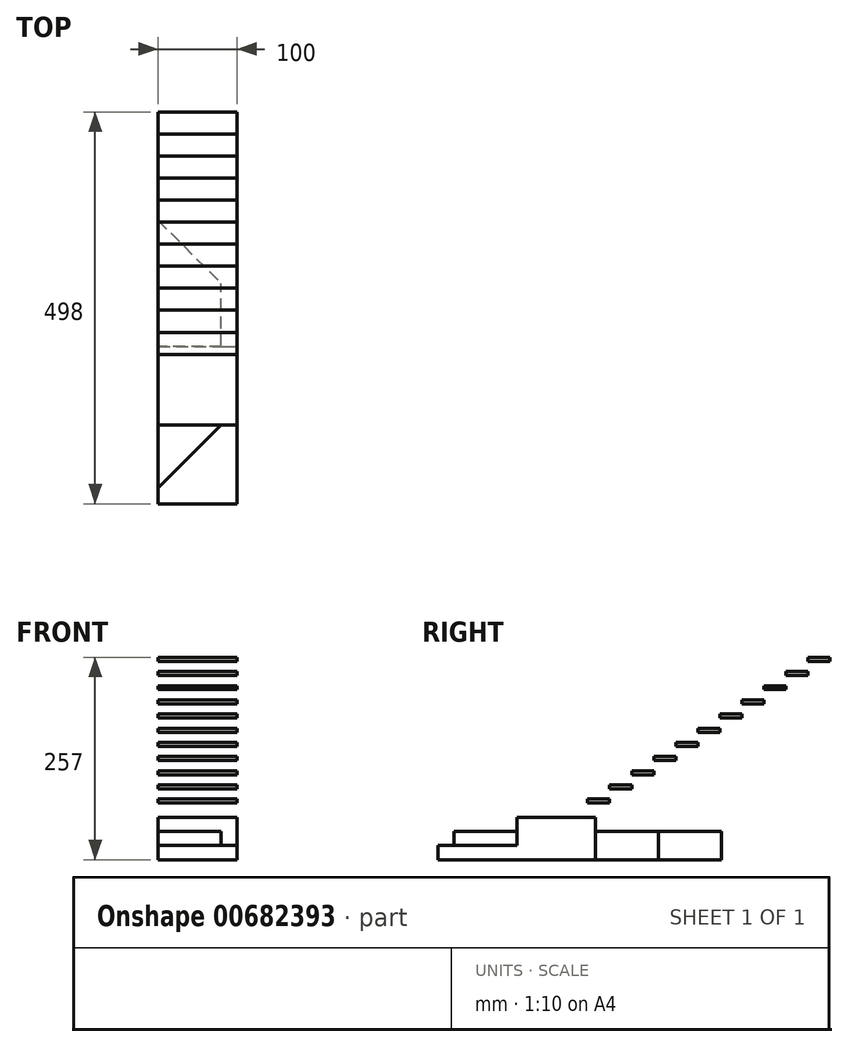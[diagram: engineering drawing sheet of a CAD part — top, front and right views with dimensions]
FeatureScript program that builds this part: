
annotation { "Feature Type Name" : "Feature", "Feature Type Description" : "" }
export const myFeature = defineFeature(function(context is Context, id is Id, definition is map)
    precondition{}
    {
        {
            var Q0;
            Q0=qCreatedBy(makeId("Right.planeOp"),FACE);
            var sketch = newSketch(context, id + "F0", { "sketchPlane" : qUnion([Q0])});
            skLineSegment(sketch, "E0.MirrorCS", {"start": v(-170, 0) * mm, "end": v(-170, 36) * mm});
            skLineSegment(sketch, "E1.MirrorCS", {"start": v(-170, 0) * mm, "end": v(0, 0) * mm});
            skLineSegment(sketch, "E2.MirrorCS", {"start": v(0, 36) * mm, "end": v(-170, 36) * mm});
            skPoint(sketch, "E3.bottom.end.orphan", {"position": v(133.33, 45) * mm});
            skPoint(sketch, "E4.left.start.orphan", {"position": v(133.33, 9) * mm});
            skPoint(sketch, "E5.right.start.orphan", {"position": v(122.85, 16.55) * mm});
            skPoint(sketch, "E5.top.end.orphan", {"position": v(122.85, 24.1) * mm});
            skPoint(sketch, "E6.right.start.orphan", {"position": v(112.37, 24.1) * mm});
            skPoint(sketch, "E6.top.end.orphan", {"position": v(112.37, 45) * mm});
            skPoint(sketch, "E7.MirrorCS.end.orphan", {"position": v(-112.37, 36) * mm});
            skPoint(sketch, "E7.MirrorCS.start.orphan", {"position": v(-112.37, 24.1) * mm});
            skPoint(sketch, "E8.MirrorCS.end.orphan", {"position": v(-122.85, 24.1) * mm});
            skPoint(sketch, "E9.MirrorCS.end.orphan", {"position": v(-122.85, 16.55) * mm});
            skPoint(sketch, "E10.MirrorCS.start.orphan", {"position": v(0, 24.1) * mm});
            skLineSegment(sketch, "E11.MirrorCS", {"start": v(0, 36) * mm, "end": v(170, 36) * mm});
            skLineSegment(sketch, "E12.MirrorCS", {"start": v(170, 0) * mm, "end": v(0, 0) * mm});
            skLineSegment(sketch, "E13.MirrorCS", {"start": v(170, 0) * mm, "end": v(170, 36) * mm});
            skSolve(sketch);
        }
        {
            var Q0;
            Q0=qSketchRegion(id+"F0",true);
            extrude(context, id + "F1", {"entities" : qUnion([Q0]), "oppositeDirection" : true, "depth" : 100 * mm, "offsetDistance" : 25 * mm, "hasSecondDirection" : true, "secondDirectionOppositeDirection" : true, "secondDirectionDepth" : 20 * mm});
        }
        {
            var Q0;
            Q0=qCreatedBy(makeId("Right.planeOp"),FACE);
            var sketch = newSketch(context, id + "F2", { "sketchPlane" : qUnion([Q0])});
            skLineSegment(sketch, "E14", {"start": v(0, 72) * mm, "end": v(28, 72) * mm});
            skLineSegment(sketch, "E15", {"start": v(28, 72) * mm, "end": v(28, 90) * mm, "construction": true});
            skLineSegment(sketch, "E16", {"start": v(28, 90) * mm, "end": v(56, 90) * mm});
            skLineSegment(sketch, "E17", {"start": v(56, 90) * mm, "end": v(56, 108) * mm, "construction": true});
            skLineSegment(sketch, "E18", {"start": v(56, 108) * mm, "end": v(84, 108) * mm});
            skLineSegment(sketch, "E19", {"start": v(84, 108) * mm, "end": v(84, 126) * mm, "construction": true});
            skLineSegment(sketch, "E20", {"start": v(84, 126) * mm, "end": v(112, 126) * mm});
            skLineSegment(sketch, "E21", {"start": v(112, 126) * mm, "end": v(112, 144) * mm, "construction": true});
            skLineSegment(sketch, "E22", {"start": v(112, 144) * mm, "end": v(140, 144) * mm});
            skLineSegment(sketch, "E23", {"start": v(140, 144) * mm, "end": v(140, 162) * mm, "construction": true});
            skLineSegment(sketch, "E24", {"start": v(140, 162) * mm, "end": v(168, 162) * mm});
            skLineSegment(sketch, "E25", {"start": v(168, 162) * mm, "end": v(168, 180) * mm, "construction": true});
            skLineSegment(sketch, "E26", {"start": v(168, 180) * mm, "end": v(196, 180) * mm});
            skLineSegment(sketch, "E27", {"start": v(196, 180) * mm, "end": v(196, 198) * mm, "construction": true});
            skLineSegment(sketch, "E28", {"start": v(196, 198) * mm, "end": v(224, 198) * mm});
            skLineSegment(sketch, "E29", {"start": v(224, 198) * mm, "end": v(224, 216) * mm, "construction": true});
            skLineSegment(sketch, "E30", {"start": v(224, 216) * mm, "end": v(252, 216) * mm});
            skLineSegment(sketch, "E31", {"start": v(252, 216) * mm, "end": v(252, 234) * mm, "construction": true});
            skLineSegment(sketch, "E32", {"start": v(252, 234) * mm, "end": v(280, 234) * mm});
            skLineSegment(sketch, "E33", {"start": v(280, 234) * mm, "end": v(280, 252) * mm, "construction": true});
            skLineSegment(sketch, "E34", {"start": v(280, 252) * mm, "end": v(308, 252) * mm});
            skLineSegment(sketch, "E35.0.1.0", {"start": v(280, 239) * mm, "end": v(280, 257) * mm, "construction": true});
            skLineSegment(sketch, "E35.0.1.1", {"start": v(252, 221) * mm, "end": v(252, 239) * mm, "construction": true});
            skLineSegment(sketch, "E35.0.1.2", {"start": v(196, 185) * mm, "end": v(196, 203) * mm, "construction": true});
            skLineSegment(sketch, "E35.0.1.3", {"start": v(84, 131) * mm, "end": v(112, 131) * mm});
            skLineSegment(sketch, "E35.0.1.4", {"start": v(252, 239) * mm, "end": v(280, 239) * mm});
            skLineSegment(sketch, "E35.0.1.5", {"start": v(280, 257) * mm, "end": v(308, 257) * mm});
            skLineSegment(sketch, "E35.0.1.6", {"start": v(196, 203) * mm, "end": v(224, 203) * mm});
            skLineSegment(sketch, "E35.0.1.7", {"start": v(168, 185) * mm, "end": v(196, 185) * mm});
            skLineSegment(sketch, "E35.0.1.8", {"start": v(168, 167) * mm, "end": v(168, 185) * mm, "construction": true});
            skLineSegment(sketch, "E35.0.1.9", {"start": v(140, 167) * mm, "end": v(168, 167) * mm});
            skLineSegment(sketch, "E35.0.1.10", {"start": v(224, 203) * mm, "end": v(224, 221) * mm, "construction": true});
            skLineSegment(sketch, "E35.0.1.11", {"start": v(140, 149) * mm, "end": v(140, 167) * mm, "construction": true});
            skLineSegment(sketch, "E35.0.1.12", {"start": v(0, 77) * mm, "end": v(28, 77) * mm});
            skLineSegment(sketch, "E35.0.1.13", {"start": v(112, 149) * mm, "end": v(140, 149) * mm});
            skLineSegment(sketch, "E35.0.1.14", {"start": v(224, 221) * mm, "end": v(252, 221) * mm});
            skLineSegment(sketch, "E35.0.1.15", {"start": v(28, 77) * mm, "end": v(28, 95) * mm, "construction": true});
            skLineSegment(sketch, "E35.0.1.16", {"start": v(28, 95) * mm, "end": v(56, 95) * mm});
            skLineSegment(sketch, "E35.0.1.17", {"start": v(112, 131) * mm, "end": v(112, 149) * mm, "construction": true});
            skLineSegment(sketch, "E35.0.1.18", {"start": v(56, 95) * mm, "end": v(56, 113) * mm, "construction": true});
            skLineSegment(sketch, "E35.0.1.19", {"start": v(56, 113) * mm, "end": v(84, 113) * mm});
            skLineSegment(sketch, "E35.0.1.20", {"start": v(84, 113) * mm, "end": v(84, 131) * mm, "construction": true});
            skLineSegment(sketch, "E35.direction1", {"start": v(-27.12, 72) * mm, "end": v(0, 72) * mm, "construction": true});
            skLineSegment(sketch, "E35.direction2", {"start": v(0, 72) * mm, "end": v(0, 77) * mm, "construction": true});
            skLineSegment(sketch, "E36", {"start": v(308, 257) * mm, "end": v(308, 252) * mm});
            skLineSegment(sketch, "E37", {"start": v(280, 257) * mm, "end": v(280, 252) * mm});
            skLineSegment(sketch, "E38", {"start": v(280, 239) * mm, "end": v(280, 234) * mm});
            skLineSegment(sketch, "E39", {"start": v(252, 239) * mm, "end": v(252, 234) * mm});
            skLineSegment(sketch, "E40", {"start": v(252, 221) * mm, "end": v(252, 216) * mm});
            skLineSegment(sketch, "E41", {"start": v(224, 221) * mm, "end": v(224, 216) * mm});
            skLineSegment(sketch, "E42", {"start": v(224, 203) * mm, "end": v(224, 198) * mm});
            skLineSegment(sketch, "E43", {"start": v(196, 203) * mm, "end": v(196, 198) * mm});
            skLineSegment(sketch, "E44", {"start": v(196, 185) * mm, "end": v(196, 180) * mm});
            skLineSegment(sketch, "E45", {"start": v(168, 185) * mm, "end": v(168, 180) * mm});
            skLineSegment(sketch, "E46", {"start": v(168, 167) * mm, "end": v(168, 162) * mm});
            skLineSegment(sketch, "E47", {"start": v(140, 167) * mm, "end": v(140, 162) * mm});
            skLineSegment(sketch, "E48", {"start": v(140, 149) * mm, "end": v(140, 144) * mm});
            skLineSegment(sketch, "E49", {"start": v(112, 149) * mm, "end": v(112, 144) * mm});
            skLineSegment(sketch, "E50", {"start": v(112, 131) * mm, "end": v(112, 126) * mm});
            skLineSegment(sketch, "E51", {"start": v(84, 131) * mm, "end": v(84, 126) * mm});
            skLineSegment(sketch, "E52", {"start": v(84, 113) * mm, "end": v(84, 108) * mm});
            skLineSegment(sketch, "E53", {"start": v(56, 113) * mm, "end": v(56, 108) * mm});
            skLineSegment(sketch, "E54", {"start": v(56, 95) * mm, "end": v(56, 90) * mm});
            skLineSegment(sketch, "E55", {"start": v(28, 95) * mm, "end": v(28, 90) * mm});
            skLineSegment(sketch, "E56", {"start": v(28, 77) * mm, "end": v(28, 72) * mm});
            skLineSegment(sketch, "E57", {"start": v(0, 77) * mm, "end": v(0, 72) * mm});
            skSolve(sketch);
        }
        {
            var Q0;
            Q0=qSketchRegion(id+"F2",true);
            extrude(context, id + "F3", {"entities" : qUnion([Q0]), "oppositeDirection" : true, "depth" : 100 * mm, "offsetDistance" : 25 * mm});
        }
        {
            var Q0;
            Q0=qCreatedBy(makeId("Right.planeOp"),FACE);
            var sketch = newSketch(context, id + "F4", { "sketchPlane" : qUnion([Q0])});
            skLineSegment(sketch, "E58.bottom", {"start": v(-190, 18) * mm, "end": v(-70, 18) * mm});
            skLineSegment(sketch, "E58.top", {"start": v(-190, 0) * mm, "end": v(-70, 0) * mm});
            skLineSegment(sketch, "E58.left", {"start": v(-190, 18) * mm, "end": v(-190, 0) * mm});
            skLineSegment(sketch, "E58.right", {"start": v(-70, 18) * mm, "end": v(-70, 0) * mm});
            skSolve(sketch);
        }
        {
            var Q0;
            Q0=makeQuery(id+"F4.imprint","IMPRINT",FACE,{"disambiguationData":[TD([[makeQuery(id+"F4.imprint","IMPRINT",EDGE,{"derivedFrom":sQuery(id+"F4.wireOp",EDGE,"E58.bottom")}),-1.0]])]});
            extrude(context, id + "F5", {"entities" : qUnion([Q0]), "operationType" : NewBodyOperationType.ADD, "oppositeDirection" : true, "depth" : 100 * mm, "offsetDistance" : 25 * mm});
        }
        {
            var Q0;
            Q0=qCreatedBy(makeId("Right.planeOp"),FACE);
            var sketch = newSketch(context, id + "F6", { "sketchPlane" : qUnion([Q0])});
            skLineSegment(sketch, "E59.bottom", {"start": v(-90, 54) * mm, "end": v(10, 54) * mm});
            skLineSegment(sketch, "E59.top", {"start": v(-90, 0) * mm, "end": v(10, 0) * mm});
            skLineSegment(sketch, "E59.left", {"start": v(-90, 54) * mm, "end": v(-90, 0) * mm});
            skLineSegment(sketch, "E59.right", {"start": v(10, 54) * mm, "end": v(10, 0) * mm});
            skSolve(sketch);
        }
        {
            var Q0;
            Q0=qSketchRegion(id+"F6",true);
            extrude(context, id + "F7", {"entities" : qUnion([Q0]), "operationType" : NewBodyOperationType.ADD, "oppositeDirection" : true, "depth" : 100 * mm, "offsetDistance" : 25 * mm});
        }
        {
            var Q0;
            {var subQ2=sQuery(id+"F0.wireOp",EDGE,"E11.MirrorCS");var subQ3=sQuery(id+"F0.wireOp",EDGE,"E2.MirrorCS");var subQ5=sQuery(id+"F0.wireOp",EDGE,"E0.MirrorCS");Q0=makeQuery(id+"F7.boolean.opBoolean","SPLIT",FACE,{"disambiguationData":[TD([makeQuery(id+"F1.opExtrude","SWEPT_FACE",FACE,{"disambiguationData":[OSD([subQ5])]})])],"derivedFrom":makeQuery(id+"F1.opExtrude","SWEPT_FACE",FACE,{"disambiguationData":[OSD([subQ3,subQ2])]})});}
            var sketch = newSketch(context, id + "F8", { "sketchPlane" : qUnion([Q0])});
            skLineSegment(sketch, "E60", {"start": v(-100, -170) * mm, "end": v(-20, -90) * mm});
            skLineSegment(sketch, "E61", {"start": v(-20, -90) * mm, "end": v(-20, -170) * mm});
            skLineSegment(sketch, "E62", {"start": v(-20, -170) * mm, "end": v(-100, -170) * mm});
            skLineSegment(sketch, "E63", {"start": v(-100, 170) * mm, "end": v(-20, 170) * mm});
            skLineSegment(sketch, "E64", {"start": v(-20, 170) * mm, "end": v(-20, 90) * mm});
            skLineSegment(sketch, "E65", {"start": v(-20, 90) * mm, "end": v(-100, 170) * mm});
            skSolve(sketch);
        }
        {
            var Q0;
            Q0=makeQuery(id+"F8.imprint","IMPRINT",FACE,{"disambiguationData":[TD([[makeQuery(id+"F8.imprint","IMPRINT",EDGE,{"derivedFrom":sQuery(id+"F8.wireOp",EDGE,"E60")}),-1.0]])]});
            extrude(context, id + "F9", {"entities" : qUnion([Q0]), "operationType" : NewBodyOperationType.REMOVE, "oppositeDirection" : true, "depth" : 18 * mm, "offsetDistance" : 25 * mm});
        }
        {
            var Q0;
            {var subQ0=sQuery(id+"F0.wireOp",EDGE,"E13.MirrorCS");var subQ2=sQuery(id+"F0.wireOp",EDGE,"E11.MirrorCS");var subQ3=sQuery(id+"F0.wireOp",EDGE,"E2.MirrorCS");Q0=makeQuery(id+"F7.boolean.opBoolean","SPLIT",FACE,{"disambiguationData":[TD([makeQuery(id+"F1.opExtrude","SWEPT_FACE",FACE,{"disambiguationData":[OSD([subQ0])]})])],"derivedFrom":makeQuery(id+"F1.opExtrude","SWEPT_FACE",FACE,{"disambiguationData":[OSD([subQ3,subQ2])]})});}
            var sketch = newSketch(context, id + "F10", { "sketchPlane" : qUnion([Q0])});
            skLineSegment(sketch, "E66", {"start": v(-100, 170) * mm, "end": v(-20, 170) * mm});
            skPoint(sketch, "E67.end.orphan", {"position": v(-100, 90) * mm});
            skLineSegment(sketch, "E68", {"start": v(-20, 170) * mm, "end": v(-20, 90) * mm});
            skLineSegment(sketch, "E69", {"start": v(-20, 90) * mm, "end": v(-100, 170) * mm});
            skSolve(sketch);
        }
        {
            var Q0;
            Q0 = qSketchRegion(id + "F10", true);
            extrude(context, id + "F11", {"entities" : qUnion([Q0]), "operationType" : NewBodyOperationType.REMOVE, "oppositeDirection" : true, "depth" : 86 * mm, "offsetDistance" : 25 * mm});
        }
    });
